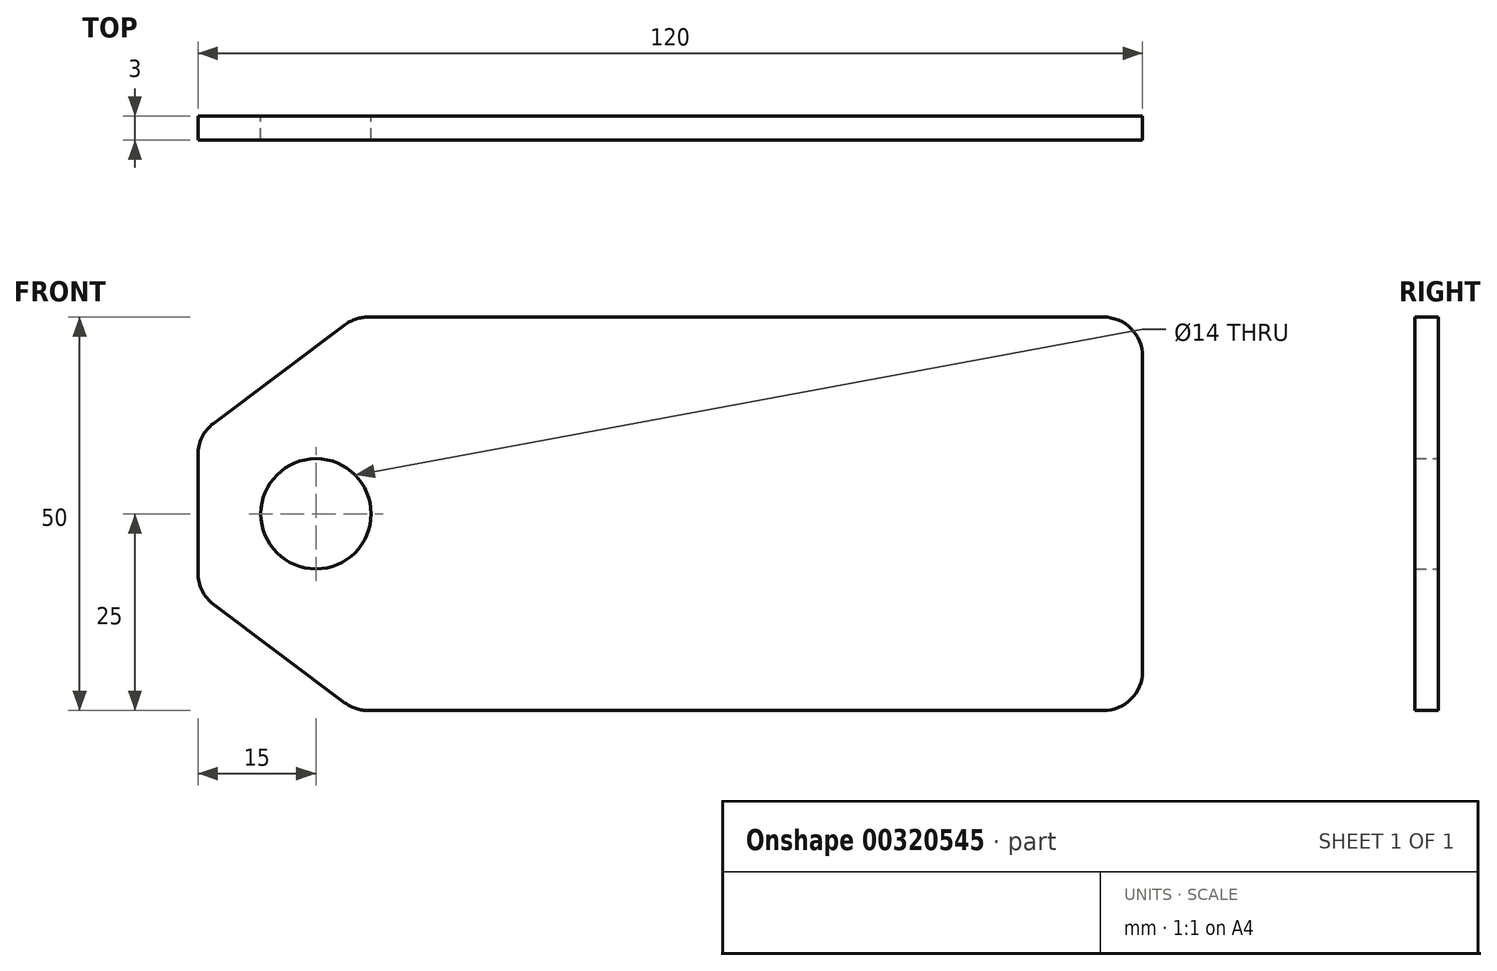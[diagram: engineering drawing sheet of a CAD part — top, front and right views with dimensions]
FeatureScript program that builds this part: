
annotation { "Feature Type Name" : "Feature", "Feature Type Description" : "" }
export const myFeature = defineFeature(function(context is Context, id is Id, definition is map)
    precondition{}
    {
        {
            var Q0;
            Q0=qCreatedBy(makeId("Front.planeOp"),FACE);
            var sketch = newSketch(context, id + "F0", { "sketchPlane" : qUnion([Q0])});
            skLineSegment(sketch, "E0.bottom", {"start": v(55, 25) * mm, "end": v(-38.33, 25) * mm});
            skLineSegment(sketch, "E0.top", {"start": v(55, -25) * mm, "end": v(-38.33, -25) * mm});
            skLineSegment(sketch, "E0.left", {"start": v(60, 20) * mm, "end": v(60, -20) * mm});
            skLineSegment(sketch, "E0.right", {"start": v(-60, 7.5) * mm, "end": v(-60, -7.5) * mm});
            skPoint(sketch, "E0.middle", {"position": v(0, 0) * mm});
            skPoint(sketch, "E1", {"position": v(-60, 10) * mm});
            skPoint(sketch, "E2", {"position": v(-60, -10) * mm});
            skPoint(sketch, "E3", {"position": v(-40, -25) * mm});
            skPoint(sketch, "E4", {"position": v(-40, 25) * mm});
            skLineSegment(sketch, "E5", {"start": v(-41.33, 24) * mm, "end": v(-58, 11.5) * mm});
            skLineSegment(sketch, "E6", {"start": v(-58, -11.5) * mm, "end": v(-41.33, -24) * mm});
            skArc(sketch, "E7.filletArc", {"start": v(-38.33, 25) * mm, "mid": v(-39.91, 24.74) * mm, "end": v(-41.33, 24) * mm});
            skArc(sketch, "E8.filletArc", {"start": v(-58, 11.5) * mm, "mid": v(-59.47, 9.74) * mm, "end": v(-60, 7.5) * mm});
            skArc(sketch, "E9.filletArc", {"start": v(-60, -7.5) * mm, "mid": v(-59.47, -9.74) * mm, "end": v(-58, -11.5) * mm});
            skArc(sketch, "E10.filletArc", {"start": v(-41.33, -24) * mm, "mid": v(-39.91, -24.74) * mm, "end": v(-38.33, -25) * mm});
            skPoint(sketch, "E11.visualSharp", {"position": v(60, -25) * mm});
            skArc(sketch, "E11.filletArc", {"start": v(55, -25) * mm, "mid": v(58.54, -23.54) * mm, "end": v(60, -20) * mm});
            skPoint(sketch, "E12.visualSharp", {"position": v(60, 25) * mm});
            skArc(sketch, "E12.filletArc", {"start": v(60, 20) * mm, "mid": v(58.54, 23.54) * mm, "end": v(55, 25) * mm});
            skPoint(sketch, "E13", {"position": v(-45, 0) * mm});
            skCircle(sketch, "E14", {"center": v(-45, 0) * mm, "radius": 7 * mm});
            skSolve(sketch);
        }
        {
            var Q0;
            Q0=makeQuery(id+"F0.imprint","IMPRINT",FACE,{"disambiguationData":[TD([[makeQuery(id+"F0.imprint","IMPRINT",EDGE,{"derivedFrom":sQuery(id+"F0.wireOp",EDGE,"E0.bottom")}),1.0]])]});
            extrude(context, id + "F1", {"entities" : qUnion([Q0]), "depth" : 3 * mm});
        }
    });
